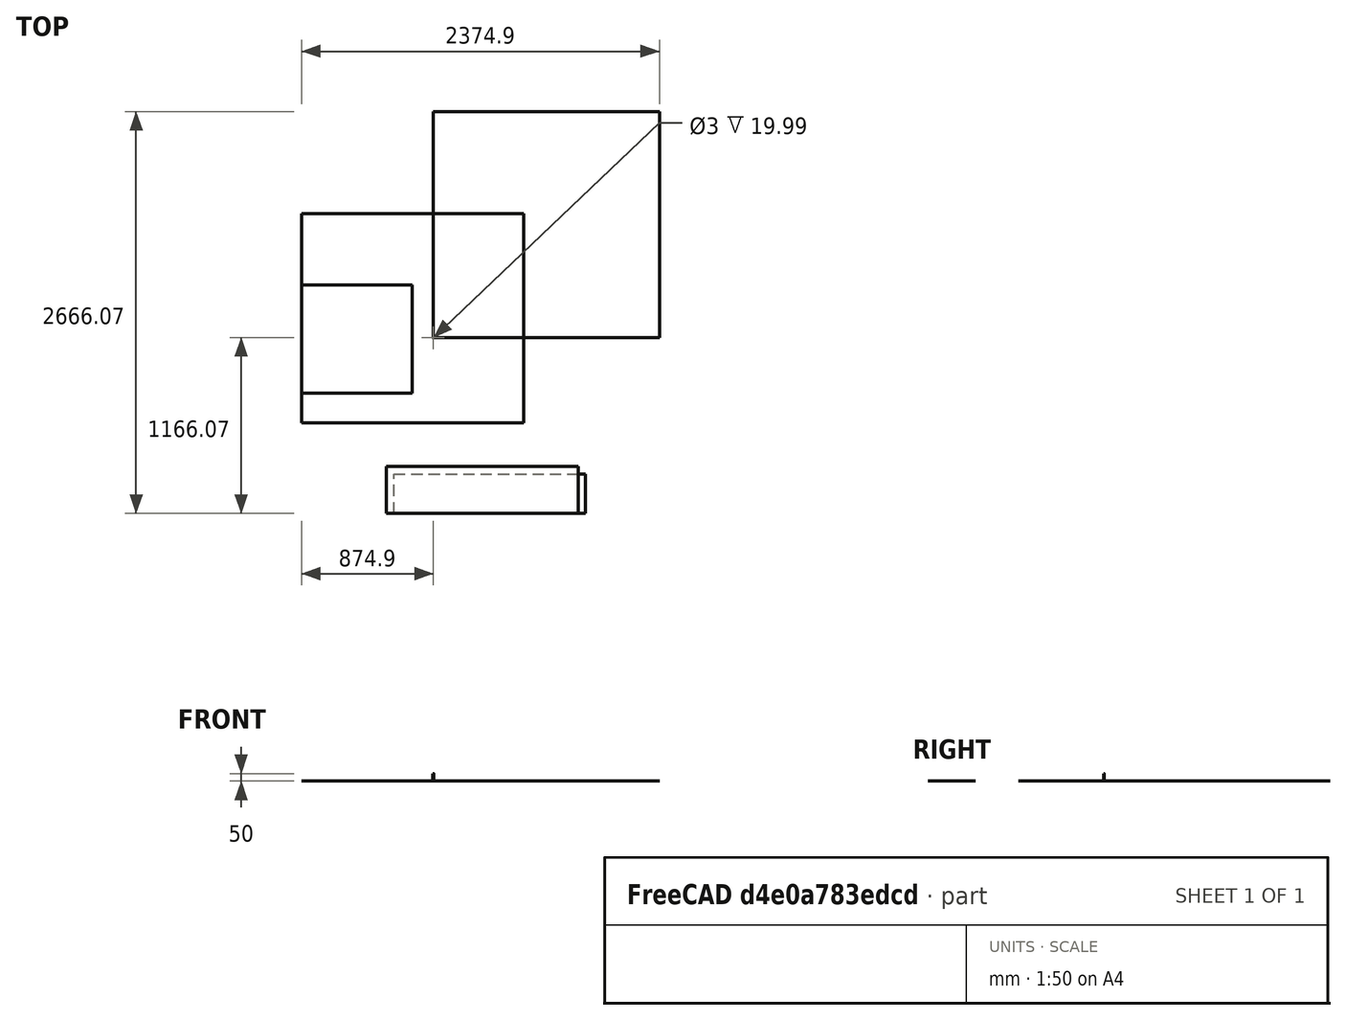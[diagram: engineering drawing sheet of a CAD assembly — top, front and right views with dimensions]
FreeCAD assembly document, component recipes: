
FREECAD ASSEMBLY — COMPONENT RECIPES ("composit_stand9_composit_cut")

This assembly document has 13 components, labeled P0..P12 below (a component is one placed body or linked part). 0 of them carry a construction recipe — the FreeCAD feature program that regenerates the part from scratch, quoted from this document or its linked companion documents; the rest are supplied as boundary geometry only. No exploded tour is included for this assembly.
COMPONENT P0 — geometry summary ("electric_shield_Body"; no construction recipe available for this part):
  bounding box: 382.0 x 155.0 x 0.3 mm
  tessellated surface: 2,244 triangles
  volume: 16266 mm^3 (92% of its bounding box)
  symmetry: mirror-symmetric across its z mid-plane
COMPONENT P1 — geometry summary ("bottom_composit_Body"; no construction recipe available for this part):
  bounding box: 668.1 x 434.6 x 0.3 mm
  tessellated surface: 1,820 triangles
  volume: 84719 mm^3 (97% of its bounding box)
  symmetry: 2-fold rotationally symmetric about the y axis; mirror-symmetric across its x mid-plane, z mid-plane
COMPONENT P2 — geometry summary ("cap_outer_Body"; no construction recipe available for this part):
  bounding box: 1270.0 x 310.8 x 0.3 mm
  tessellated surface: 1,492 triangles
  volume: 65819 mm^3 (56% of its bounding box)
  symmetry: 2-fold rotationally symmetric about the x axis; mirror-symmetric across its y mid-plane, z mid-plane
COMPONENT P3 — geometry summary ("cap_inner_Body"; no construction recipe available for this part):
  bounding box: 196.9 x 179.9 x 0.3 mm
  tessellated surface: 772 triangles
  volume: 8799 mm^3 (83% of its bounding box)
  symmetry: mirror-symmetric across its z mid-plane
COMPONENT P4 — geometry summary ("front_shield_Body"; no construction recipe available for this part):
  bounding box: 639.1 x 129.0 x 1.0 mm
  tessellated surface: 508 triangles
  volume: 81312 mm^3 (99% of its bounding box)
  symmetry: 2-fold rotationally symmetric about the x axis; 2-fold rotationally symmetric about the y axis; 2-fold rotationally symmetric about the z axis; mirror-symmetric across its x mid-plane, y mid-plane, z mid-plane
COMPONENT P5 — geometry summary ("bottom_composit"; no construction recipe available for this part):
  bounding box: 639.1 x 203.0 x 18.0 mm
  tessellated surface: 2,044 triangles
  volume: 84809 mm^3 (4% of its bounding box)
  symmetry: mirror-symmetric across its x mid-plane
COMPONENT P6 — geometry summary ("electric_shield"; no construction recipe available for this part):
  bounding box: 323.0 x 96.0 x 30.0 mm
  tessellated surface: 2,340 triangles
  volume: 16289 mm^3 (2% of its bounding box)
  symmetry: 2-fold rotationally symmetric about the z axis
COMPONENT P7 — geometry summary ("cap_inner"; no construction recipe available for this part):
  bounding box: 150.0 x 127.0 x 53.4 mm
  tessellated surface: 832 triangles
  volume: 8807 mm^3 (1% of its bounding box)
COMPONENT P8 — geometry summary ("cap_outer"; no construction recipe available for this part):
  bounding box: 639.1 x 211.0 x 50.4 mm
  tessellated surface: 1,748 triangles
  volume: 65872 mm^3 (1% of its bounding box)
  symmetry: 2-fold rotationally symmetric about the z axis; mirror-symmetric across its x mid-plane, y mid-plane
COMPONENT P9 — geometry summary ("face"; no construction recipe available for this part):
  bounding box: 715.4 x 639.1 x 199.5 mm
  tessellated surface: 6,892 triangles
  volume: 219158 mm^3 (0% of its bounding box)
COMPONENT P10 — geometry summary ("dropper_fix_composit"; no construction recipe available for this part):
  bounding box: 627.9 x 195.4 x 20.4 mm
  tessellated surface: 5,756 triangles
  volume: 33667 mm^3 (1% of its bounding box)
  symmetry: mirror-symmetric across its x mid-plane
COMPONENT P11 — geometry summary ("front_shield"; no construction recipe available for this part):
  bounding box: 639.1 x 129.0 x 1.0 mm
  tessellated surface: 508 triangles
  volume: 81312 mm^3 (99% of its bounding box)
  symmetry: 2-fold rotationally symmetric about the x axis; 2-fold rotationally symmetric about the y axis; 2-fold rotationally symmetric about the z axis; mirror-symmetric across its x mid-plane, y mid-plane, z mid-plane
COMPONENT P12 — geometry summary ("back"; no construction recipe available for this part):
  bounding box: 715.4 x 633.1 x 20.4 mm
  tessellated surface: 2,304 triangles
  volume: 145514 mm^3 (2% of its bounding box)
  symmetry: mirror-symmetric across its x mid-plane
PROVENANCE & LICENSES
A FreeCAD (.FCStd) document from a public repository crawl; recipes are the document's own serialized feature recipes (and, for linked parts, companion documents' recipes).
License: as declared in the source repository (recorded in the dataset sidecar).
